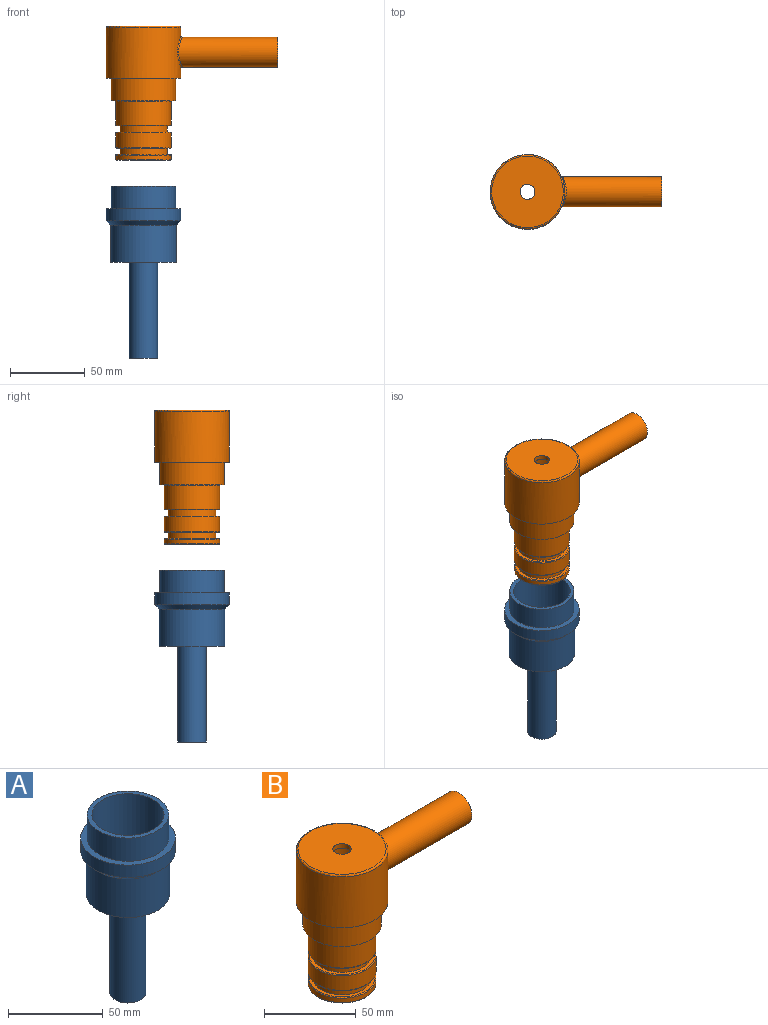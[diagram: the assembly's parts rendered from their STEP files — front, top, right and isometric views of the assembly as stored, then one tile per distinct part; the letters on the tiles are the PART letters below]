
ASSEMBLY  parts=2 mates=1
PART A: 12 faces, bbox 50x50x115 mm
  f0: plane 19x19mm, normal (0,0,-1), area 106.8mm2, adj f1,f11
  f1: cylinder r=7.5mm len=68mm, axis (0,0,-1), area 3204.4mm2, adj f0,f2
  f2: plane 38x38mm, normal (0,0,1), area 957.4mm2, adj f1,f3
  f3: cylinder r=19mm len=47mm, axis (0,0,-1), area 5610.9mm2, adj f2,f4
  f4: plane 43x43mm, normal (0,0,1), area 318.1mm2, adj f3,f5
  f5: cylinder r=21.5mm len=43mm, axis (0,0,-1), area 2026.3mm2, adj f4,f6
  f6: plane 50x50mm, normal (0,0,1), area 511.3mm2, adj f5,f7
  f7: cylinder r=25mm len=50mm, axis (0,0,-1), area 1256.6mm2, adj f6,f8
  f8: cone r=25mm half-angle=45deg, axis (0,0,1), area 626.4mm2, adj f7,f9
  f9: cylinder r=22mm len=44mm, axis (0,0,-1), area 3455.8mm2, adj f8,f10
  f10: plane 44x44mm, normal (0,0,-1), area 1237mm2, adj f9,f11
  f11: cylinder r=9.5mm len=64mm, axis (0,0,-1), area 3820.2mm2, adj f0,f10
PART B: 29 faces, bbox 117.1x54.1x90 mm
  f0: plane 36x36mm, normal (0,0,-1), area 527mm2, adj f1,f23
  f1: cylinder r=12.5mm len=87mm, axis (0,0,1), area 6557.6mm2, adj f0,f2,f25
  f2: plane 25x25mm, normal (0,0,-1), area 412.3mm2, adj f1,f3
  f3: cylinder r=5mm len=10mm, axis (0,0,1), area 94.2mm2, adj f2,f4
  f4: plane 48x48mm, normal (0,0,1), area 1731mm2, adj f3,f24
  f5: cylinder r=25mm len=50mm, axis (0,0,1), area 4965.9mm2, adj f6,f24,f28
  f6: plane 50x50mm, normal (0,0,-1), area 511.3mm2, adj f5,f7
  f7: cylinder r=21.5mm len=43mm, axis (0,0,1), area 2026.3mm2, adj f6,f8
  f8: plane 43x43mm, normal (0,0,-1), area 318.1mm2, adj f7,f18
  f9: cylinder r=18.5mm len=37mm, axis (0,0,1), area 1854mm2, adj f18,f19
  f10: plane 36x36mm, normal (0,0,-1), area 213.6mm2, adj f11,f19
  f11: cylinder r=16mm len=32mm, axis (0,0,1), area 412.2mm2, adj f10,f12
  f12: plane 36x36mm, normal (0,0,1), area 213.6mm2, adj f11,f20
  f13: cylinder r=18.5mm len=37mm, axis (0,0,1), area 1150.8mm2, adj f20,f21
  f14: plane 36x36mm, normal (0,0,-1), area 213.6mm2, adj f15,f21
  f15: cylinder r=16mm len=32mm, axis (0,0,1), area 412.1mm2, adj f14,f16
  f16: plane 36x36mm, normal (0,0,1), area 213.6mm2, adj f15,f22
  f17: cylinder r=18.5mm len=37mm, axis (0,0,1), area 342.9mm2, adj f22,f23
  f18: torus R=19mm, axis (0,0,1), area 92.2mm2, adj f8,f9
  f19: torus R=18mm, axis (0,0,1), area 90.4mm2, adj f9,f10
  f20: torus R=18mm, axis (0,0,-1), area 90.4mm2, adj f12,f13
  f21: torus R=18mm, axis (0,0,-1), area 90.4mm2, adj f13,f14
  f22: torus R=18mm, axis (0,0,-1), area 90.4mm2, adj f16,f17
  f23: torus R=18mm, axis (0,0,1), area 90.4mm2, adj f0,f17
  f24: torus R=24mm, axis (0,0,-1), area 243.2mm2, adj f4,f5
  f25: cylinder r=9mm len=81.33mm, axis (1,0,0), area 4485.8mm2, adj f1,f27
  f26: cylinder r=10mm len=66.44mm, axis (1,0,0), area 4097.1mm2, adj f27,f28
  f27: plane 20x20mm, normal (1,0,0), area 59.7mm2, adj f25,f26
  f28: bspline ~22.01x21.17mm, area 88.5mm2, adj f5,f26
PLACE A at identity
PLACE B t=(0,0,132.45)mm
MATE cylindrical B.f1 <-> A.f1  axis (0,0,1) through (0,0,156)mm
